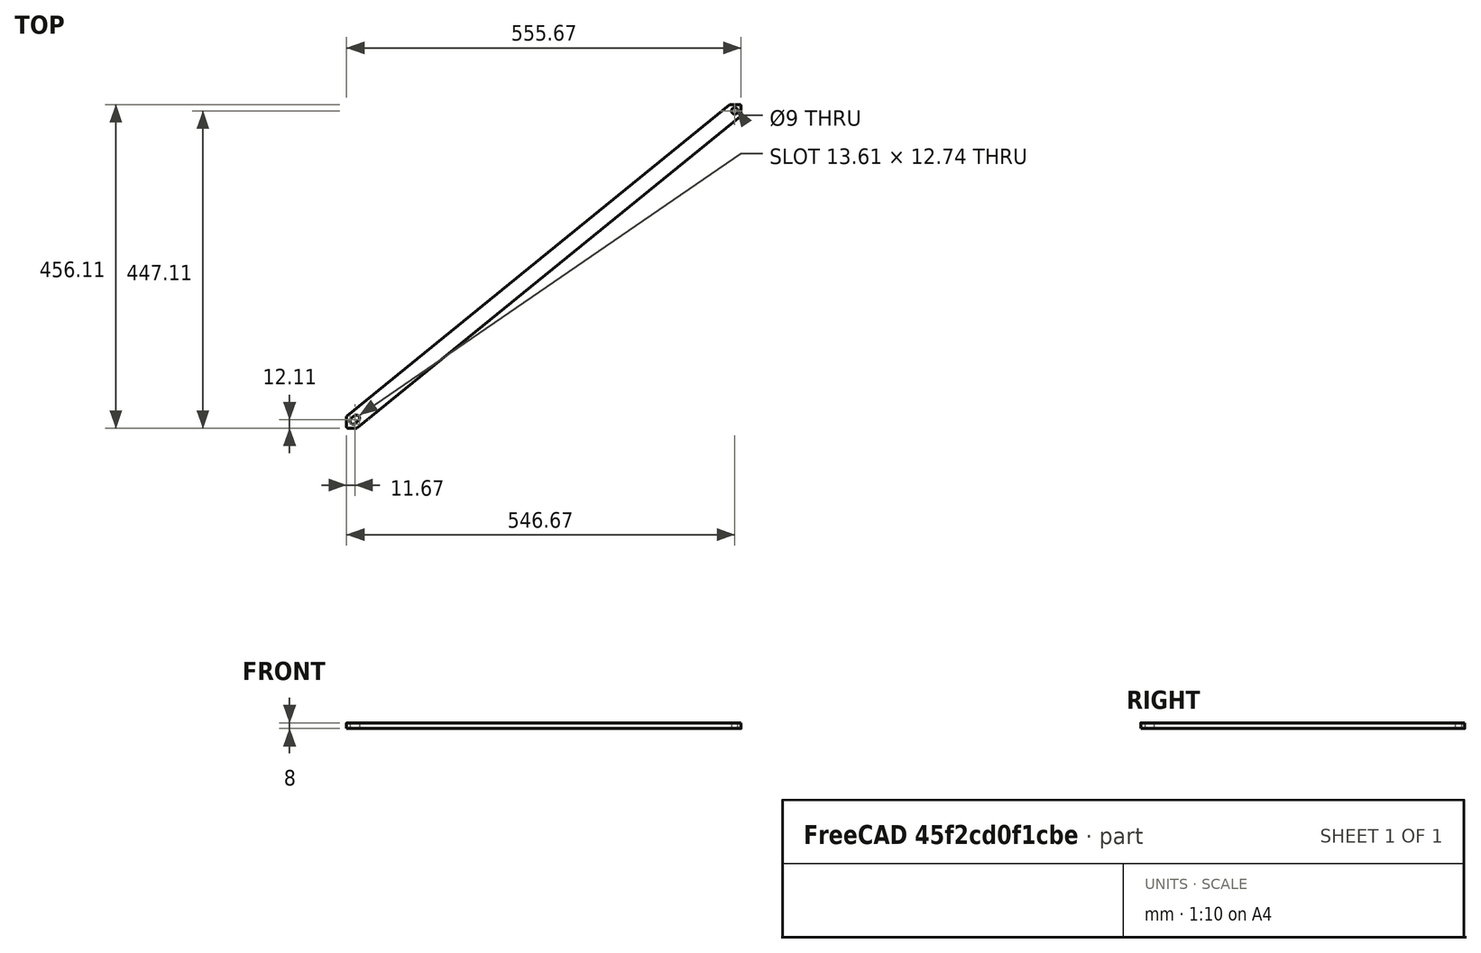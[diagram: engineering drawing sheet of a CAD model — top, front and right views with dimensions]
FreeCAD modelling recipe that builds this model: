
FCSTD DOCUMENT  (FreeCAD 0.19R24366 (Git))
Label: Diagonal brace strut to side panels
License: All rights reserved
LicenseURL: http://en.wikipedia.org/wiki/All_rights_reserved
objects: Sketcher::SketchObject×1, PartDesign::Pad×1, PartDesign::Body×1
note: 4 computed .brp shape members not serialized (recipe doc carries the construction recipe); baked Part::Feature solids carry a one-line shape summary decoded from their .brp

FEATURE [Sketcher::SketchObject] Sketch
  FullyConstrained = true
  MapMode = 5
  Support = -> [XY_Plane]
  sketch-geometry (26):
    g0: GeomPoint X=0 Y=630 Z=0
    g1: GeomPoint X=-28 Y=610 Z=0
    g2: GeomPoint X=-563 Y=175 Z=0
    g3: LineSegment StartX=-28 StartY=610 StartZ=0 EndX=-563 EndY=175 EndZ=0
    g4: Circle CenterX=-28 CenterY=610 CenterZ=0 NormalX=0 NormalY=0 NormalZ=1 AngleXU=0 Radius=4.5
    g5: Circle CenterX=-563 CenterY=175 CenterZ=0 NormalX=0 NormalY=0 NormalZ=1 AngleXU=0 Radius=4.5
    g6: LineSegment StartX=-30.8389 StartY=613.492 StartZ=0 EndX=-25.1611 EndY=606.508 EndZ=0
    g7: LineSegment StartX=-560.161 StartY=171.508 StartZ=0 EndX=-565.839 EndY=178.492 EndZ=0
    g8: LineSegment StartX=-563.511 StartY=180.384 StartZ=0 EndX=-568.167 EndY=176.599 EndZ=0
    g9: LineSegment StartX=-557.833 StartY=173.401 StartZ=0 EndX=-562.489 EndY=169.616 EndZ=0
    g10: LineSegment StartX=-34.9186 StartY=618.552 StartZ=0 EndX=-573.934 EndY=180.287 EndZ=0
    g11: LineSegment StartX=-559.903 StartY=163.341 StartZ=0 EndX=-19.7383 EndY=602.54 EndZ=0
    g12: LineSegment StartX=-25.1611 StartY=606.508 StartZ=0 EndX=-21.0605 EndY=601.465 EndZ=0
    g13: LineSegment StartX=-30.8389 StartY=613.492 StartZ=0 EndX=-34.9395 EndY=618.535 EndZ=0
    g14: ArcOfCircle CenterX=-33.6569 CenterY=617 CenterZ=0 NormalX=0 NormalY=0 NormalZ=1 AngleXU=0 Radius=2 StartAngle=1.5708 EndAngle=2.25346
    g15: ArcOfCircle CenterX=-21 CenterY=604.092 CenterZ=0 NormalX=0 NormalY=0 NormalZ=1 AngleXU=0 Radius=2 StartAngle=5.39506 EndAngle=6.28319
    g16: LineSegment StartX=-561.165 StartY=162.893 StartZ=0 EndX=-572.672 EndY=162.893 EndZ=0
    g17: ArcOfCircle CenterX=-572.672 CenterY=178.735 CenterZ=0 NormalX=0 NormalY=0 NormalZ=1 AngleXU=0 Radius=2 StartAngle=2.25346 EndAngle=3.14159
    g18: ArcOfCircle CenterX=-572.672 CenterY=164.893 CenterZ=0 NormalX=0 NormalY=0 NormalZ=1 AngleXU=0 Radius=2 StartAngle=3.14159 EndAngle=4.71239
    g19: ArcOfCircle CenterX=-561.165 CenterY=164.893 CenterZ=0 NormalX=0 NormalY=0 NormalZ=1 AngleXU=0 Radius=2 StartAngle=4.71239 EndAngle=5.39506
    g20: ArcOfCircle CenterX=-560.672 CenterY=176.893 CenterZ=0 NormalX=0 NormalY=0 NormalZ=1 AngleXU=0 Radius=4.5 StartAngle=5.39506 EndAngle=8.53665
    g21: ArcOfCircle CenterX=-565.328 CenterY=173.107 CenterZ=0 NormalX=0 NormalY=0 NormalZ=1 AngleXU=0 Radius=4.5 StartAngle=2.25346 EndAngle=5.39506
    g22: LineSegment StartX=-574.672 StartY=178.735 StartZ=0 EndX=-574.672 EndY=164.893 EndZ=0
    g23: LineSegment StartX=-33.6569 StartY=619 StartZ=0 EndX=-21 EndY=619 EndZ=0
    g24: LineSegment StartX=-19 StartY=604.092 StartZ=0 EndX=-19 EndY=617 EndZ=0
    g25: ArcOfCircle CenterX=-21 CenterY=617 CenterZ=0 NormalX=0 NormalY=0 NormalZ=1 AngleXU=0 Radius=2 StartAngle=-3.82e-14 EndAngle=1.5708
  constraints (66):
    c: PointOnObject(g0,g-2)
    c: DistanceY(g-1,g0) = 630
    c: DistanceY(g1,g0) = 20
    c: DistanceY(g-1,g2) = 175
    c: Coincident(g3,g1)
    c: Coincident(g4,g3)
    c: Coincident(g5,g3)
    c: Equal(g5,g4)
    c: Radius(g4) = 4.5
    c: PointOnObject(g6,g4)
    c: PointOnObject(g6,g4)
    c: PointOnObject(g3,g6)
    c: Perpendicular(g3,g6)
    c: PointOnObject(g7,g5)
    c: PointOnObject(g7,g5)
    c: PointOnObject(g3,g7)
    c: Perpendicular(g3,g7)
    c: Coincident(g3,g2)
    c: Parallel(g8,g3)
    c: Parallel(g3,g9)
    c: Symmetric(g8,g8,g7)
    c: Symmetric(g9,g9,g7)
    c: Equal(g9,g8)
    c: Coincident(g12,g6)
    c: PointOnObject(g12,g11)
    c: Coincident(g13,g6)
    c: PointOnObject(g13,g10)
    c: Parallel(g6,g12)
    c: Parallel(g12,g13)
    c: Equal(g13,g12)
    c: Distance(g12,g13) = 22
    c: Tangent(g10,g14) = -1.5708
    c: Tangent(g11,g15) = -1.5708
    c: Tangent(g10,g17) = -1.5708
    c: Tangent(g16,g18) = 1.5708
    c: Tangent(g11,g19) = -1.5708
    c: Tangent(g16,g19) = 1.5708
    c: Equal(g19,g18)
    c: Equal(g18,g17)
    c: Equal(g17,g14)
    c: Distance(g9) = 6
    c: Parallel(g11,g3)
    c: Parallel(g3,g10)
    c: Coincident(g20,g8)
    c: Coincident(g21,g8)
    c: Tangent(g20,g9) = 1.5708
    c: Tangent(g21,g9) = 1.5708
    c: Horizontal(g16)
    c: Tangent(g22,g17) = -1.5708
    c: Tangent(g22,g18) = -1.5708
    c: Vertical(g22)
    c: DistanceX(g2,g-1) = 563
    c: DistanceX(g4,g-1) = 28
    c: Horizontal(g23)
    c: Radius(g14) = 2
    c: Tangent(g23,g14) = 1.5708
    c: Tangent(g24,g15) = -1.5708
    c: Tangent(g24,g25) = -1.5708
    c: Tangent(g23,g25) = 1.5708
    c: Equal(g25,g14)
    c: Vertical(g24)
    c: Equal(g15,g14)
    c: DistanceX(g4,g24) = 9
    c: DistanceY(g4,g23) = 9
    c: DistanceX(g17,g20) = 14
    c: DistanceY(g16,g20) = 14
FEATURE [PartDesign::Pad] Pad
  Direction = (1,1,1)
  Length = 8
  Length2 = 100
  Profile = -> Sketch
  Type = 0
FEATURE [PartDesign::Body] Body
  Group = -> [Sketch,Pad]
  Origin = -> Origin
  Tip = -> Pad
